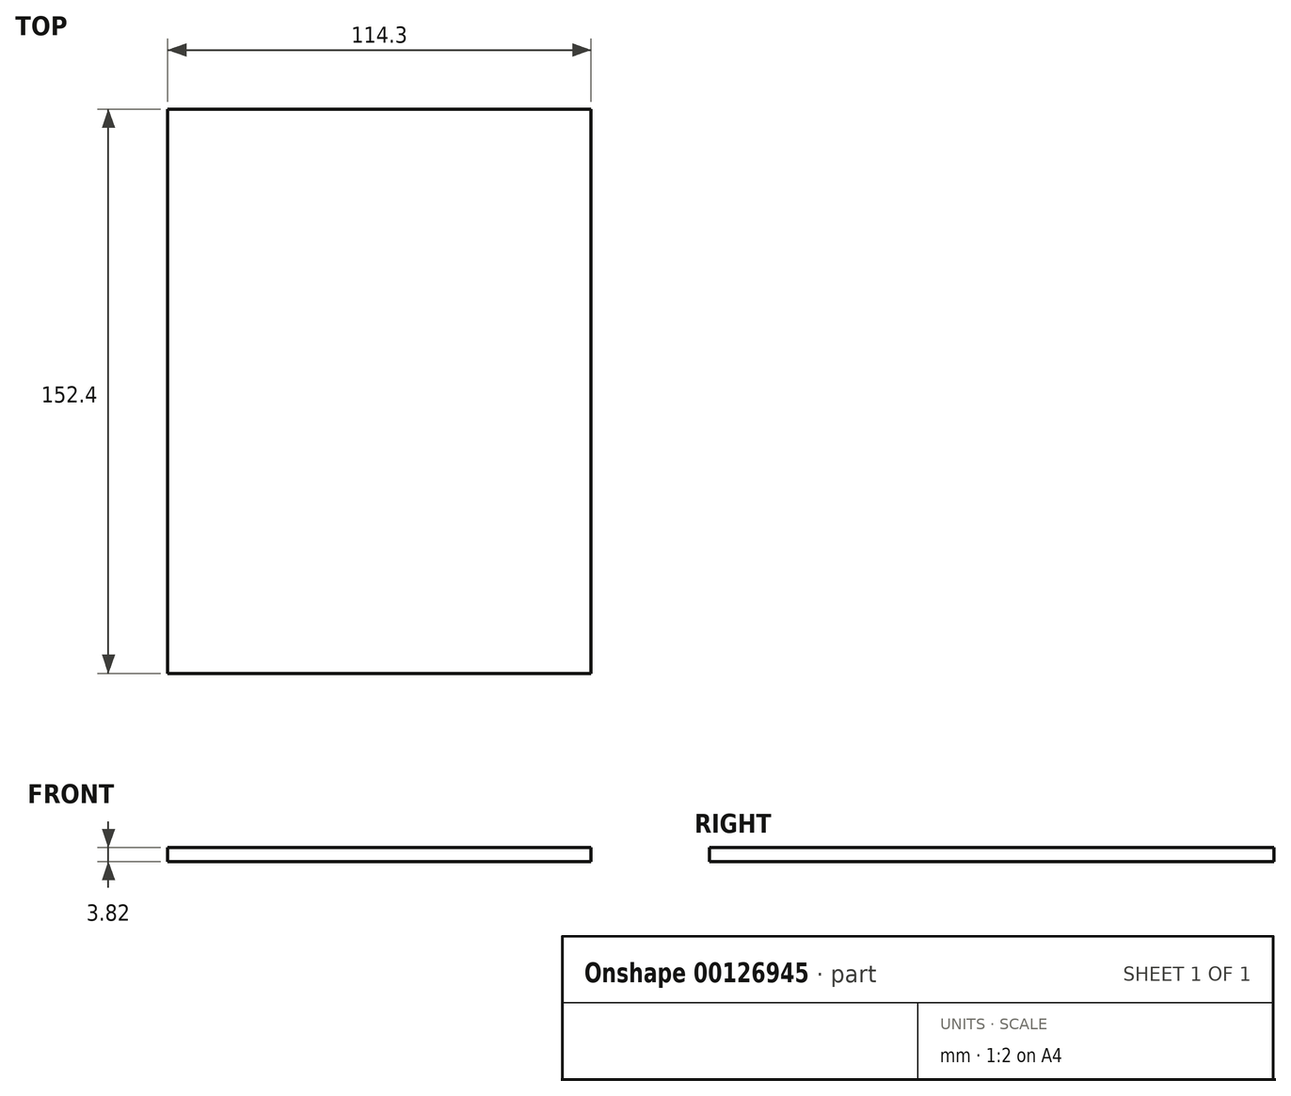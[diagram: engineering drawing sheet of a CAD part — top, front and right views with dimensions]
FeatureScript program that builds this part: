
annotation { "Feature Type Name" : "Feature", "Feature Type Description" : "" }
export const myFeature = defineFeature(function(context is Context, id is Id, definition is map)
    precondition{}
    {
        {
            var Q0;
            Q0=qCreatedBy(makeId("Front.planeOp"),FACE);
            var sketch = newSketch(context, id + "F0", { "sketchPlane" : qUnion([Q0])});
            skLineSegment(sketch, "E0.top", {"start": v(57.15, -1.9) * mm, "end": v(-57.15, -1.9) * mm});
            skLineSegment(sketch, "E0.left", {"start": v(57.15, 1.9) * mm, "end": v(57.15, -1.9) * mm});
            skLineSegment(sketch, "E0.right", {"start": v(-57.15, 1.9) * mm, "end": v(-57.15, -1.9) * mm});
            skPoint(sketch, "E0.middle", {"position": v(0, 0) * mm});
            skLineSegment(sketch, "E1", {"start": v(-57.15, 1.9) * mm, "end": v(57.15, 1.9) * mm});
            skSolve(sketch);
        }
        {
            var Q0;
            Q0=makeQuery(id+"F0.imprint","IMPRINT",FACE,{"disambiguationData":[TD([[makeQuery(id+"F0.imprint","IMPRINT",EDGE,{"derivedFrom":sQuery(id+"F0.wireOp",EDGE,"E0.top")}),-1.0]])]});
            extrude(context, id + "F1", {"entities" : qUnion([Q0]), "depth" : 152.4 * mm});
        }
    });
